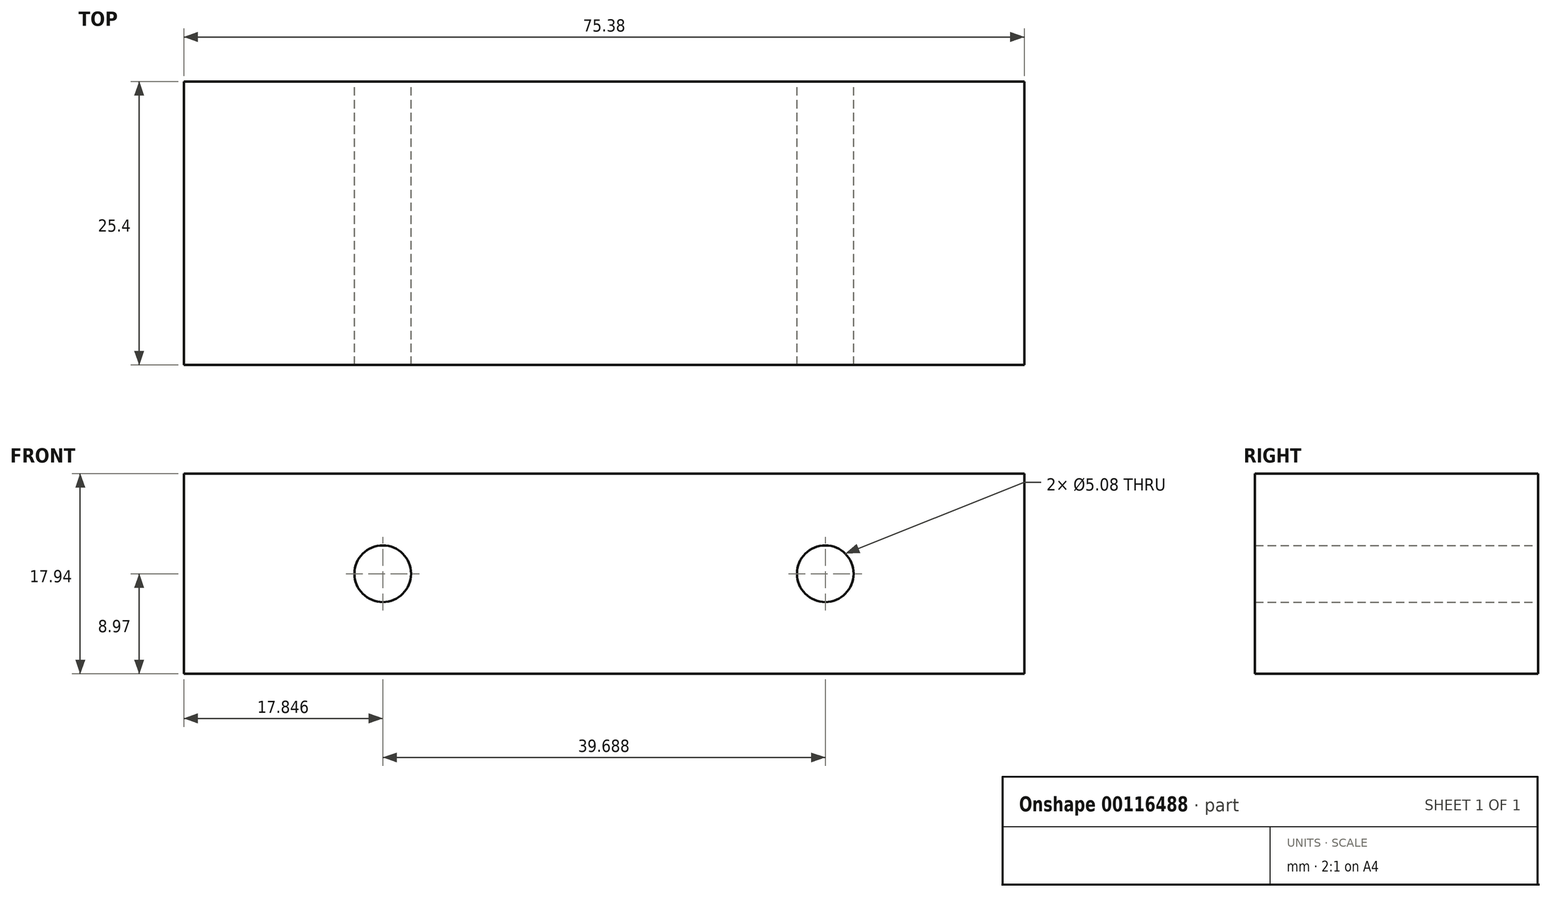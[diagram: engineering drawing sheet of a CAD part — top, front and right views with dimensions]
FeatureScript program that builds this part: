
annotation { "Feature Type Name" : "Feature", "Feature Type Description" : "" }
export const myFeature = defineFeature(function(context is Context, id is Id, definition is map)
    precondition{}
    {
        {
            var Q0;
            Q0=qCreatedBy(makeId("Front.planeOp"),FACE);
            var sketch = newSketch(context, id + "F0", { "sketchPlane" : qUnion([Q0])});
            skLineSegment(sketch, "E0.bottom", {"start": v(-19.84, 8.97) * mm, "end": v(19.84, 8.97) * mm});
            skLineSegment(sketch, "E0.top", {"start": v(-19.84, -8.97) * mm, "end": v(19.84, -8.97) * mm});
            skPoint(sketch, "E0.middle", {"position": v(0, 0) * mm});
            skLineSegment(sketch, "E1.bottom", {"start": v(-19.84, 8.97) * mm, "end": v(-37.69, 8.97) * mm});
            skLineSegment(sketch, "E1.top", {"start": v(-19.84, -8.97) * mm, "end": v(-37.69, -8.97) * mm});
            skLineSegment(sketch, "E1.right", {"start": v(-37.69, 8.97) * mm, "end": v(-37.69, -8.97) * mm});
            skLineSegment(sketch, "E2.bottom", {"start": v(19.84, 8.97) * mm, "end": v(37.69, 8.97) * mm});
            skLineSegment(sketch, "E2.top", {"start": v(19.84, -8.97) * mm, "end": v(37.69, -8.97) * mm});
            skLineSegment(sketch, "E2.right", {"start": v(37.69, 8.97) * mm, "end": v(37.69, -8.97) * mm});
            skPoint(sketch, "E3", {"position": v(-19.84, 0) * mm});
            skPoint(sketch, "E4", {"position": v(19.84, 0) * mm});
            skCircle(sketch, "E5", {"center": v(-19.84, 0) * mm, "radius": 2.54 * mm});
            skCircle(sketch, "E6", {"center": v(19.84, 0) * mm, "radius": 2.54 * mm});
            skLineSegment(sketch, "E7.trimOffspring", {"start": v(-19.84, -8.97) * mm, "end": v(-19.84, -8.97) * mm});
            skLineSegment(sketch, "E8.trimOffspring", {"start": v(19.84, -8.97) * mm, "end": v(19.84, -8.97) * mm});
            skSolve(sketch);
        }
        {
            var Q0;
            Q0=makeQuery(id+"F0.imprint","IMPRINT",FACE,{"disambiguationData":[TD([[makeQuery(id+"F0.imprint","IMPRINT",EDGE,{"derivedFrom":sQuery(id+"F0.wireOp",EDGE,"E0.bottom")}),-1.0]])]});
            extrude(context, id + "F1", {"entities" : qUnion([Q0]), "depth" : 25.4 * mm});
        }
    });
